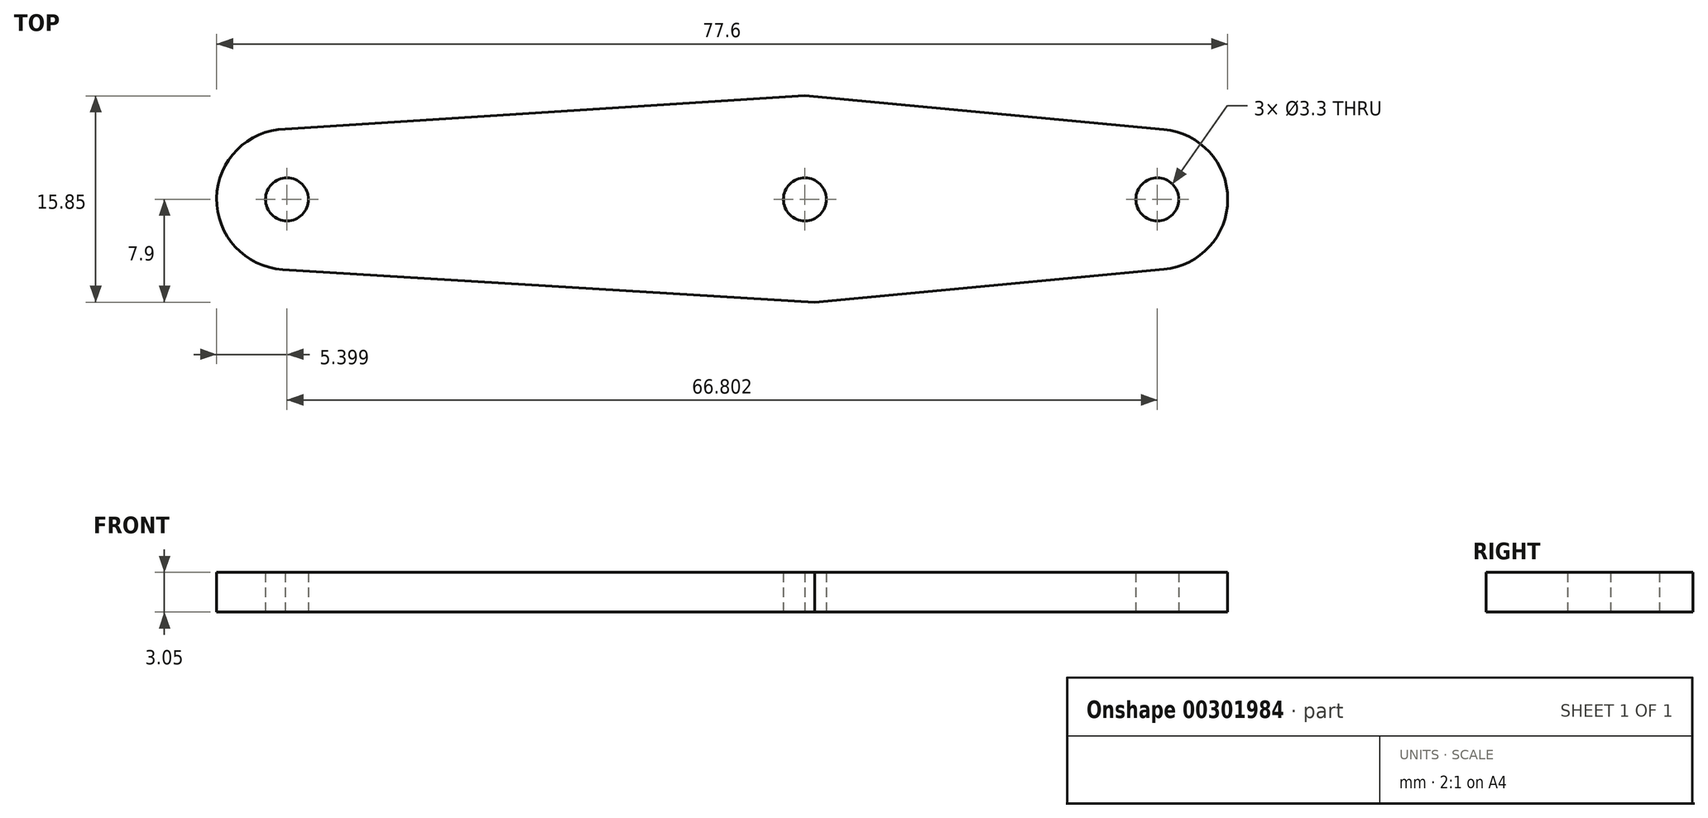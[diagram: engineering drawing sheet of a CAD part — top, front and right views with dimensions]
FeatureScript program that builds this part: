
annotation { "Feature Type Name" : "Feature", "Feature Type Description" : "" }
export const myFeature = defineFeature(function(context is Context, id is Id, definition is map)
    precondition{}
    {
        {
            var Q0;
            Q0=qCreatedBy(makeId("Top.planeOp"),FACE);
            var sketch = newSketch(context, id + "F0", { "sketchPlane" : qUnion([Q0])});
            skCircle(sketch, "E0", {"center": v(-39.75, 0) * mm, "radius": 5.4 * mm});
            skCircle(sketch, "E1", {"center": v(27.05, 0) * mm, "radius": 5.4 * mm});
            skLineSegment(sketch, "E2", {"start": v(-39.9, 5.4) * mm, "end": v(0, 7.95) * mm});
            skLineSegment(sketch, "E3", {"start": v(0, 7.95) * mm, "end": v(27.55, 5.37) * mm});
            skLineSegment(sketch, "E4", {"start": v(27.55, -5.37) * mm, "end": v(0.75, -7.9) * mm});
            skLineSegment(sketch, "E5", {"start": v(0.75, -7.9) * mm, "end": v(-40.08, -5.39) * mm});
            skCircle(sketch, "E6", {"center": v(-39.75, 0) * mm, "radius": 1.65 * mm});
            skCircle(sketch, "E7", {"center": v(0, 0) * mm, "radius": 1.65 * mm});
            skCircle(sketch, "E8", {"center": v(27.05, 0) * mm, "radius": 1.65 * mm});
            skSolve(sketch);
        }
        {
            var Q0;
            Q0 = qSketchRegion(id + "F0", true);
            var Q1;
            {var subQ1=sQuery(id+"F0.wireOp",EDGE,"E2");Q1=makeQuery(id+"F0.imprint","IMPRINT",FACE,{"disambiguationData":[TD([[makeQuery(id+"F0.imprint","IMPRINT",EDGE,{"derivedFrom":subQ1}),-1.0]])]});}
            extrude(context, id + "F1", {"entities" : qUnion([Q0, Q1]), "depth" : 3.05 * mm});
        }
    });
